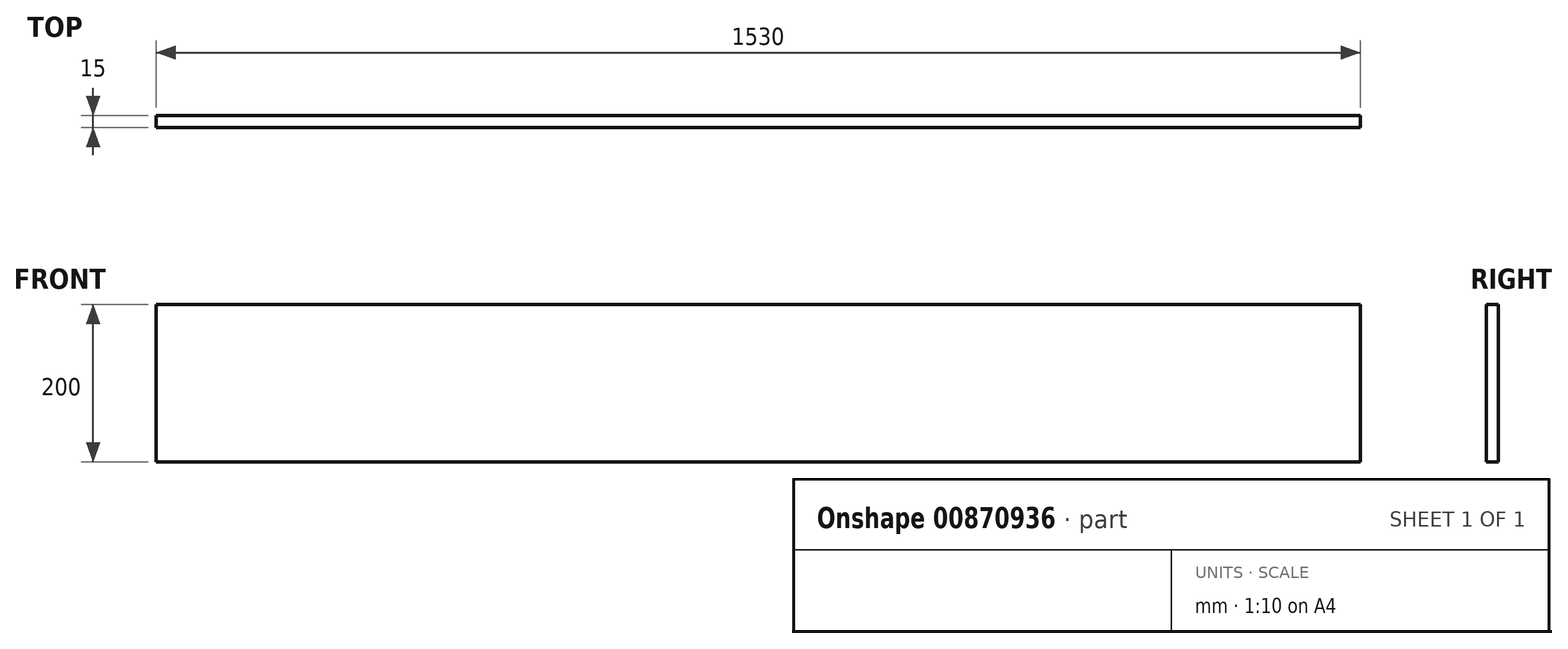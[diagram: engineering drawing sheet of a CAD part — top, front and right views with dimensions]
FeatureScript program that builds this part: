
annotation { "Feature Type Name" : "Feature", "Feature Type Description" : "" }
export const myFeature = defineFeature(function(context is Context, id is Id, definition is map)
    precondition{}
    {
        {
            var Q0;
            Q0=qCreatedBy(makeId("Front.planeOp"),FACE);
            var sketch = newSketch(context, id + "F0", { "sketchPlane" : qUnion([Q0])});
            skLineSegment(sketch, "E0.bottom", {"start": v(0, 0) * mm, "end": v(-1530, 0) * mm});
            skLineSegment(sketch, "E0.top", {"start": v(0, 200) * mm, "end": v(-1530, 200) * mm});
            skLineSegment(sketch, "E0.left", {"start": v(0, 0) * mm, "end": v(0, 200) * mm});
            skLineSegment(sketch, "E0.right", {"start": v(-1530, 0) * mm, "end": v(-1530, 200) * mm});
            skPoint(sketch, "E0.middle", {"position": v(-765, 100) * mm});
            skSolve(sketch);
        }
        {
            var Q0;
            Q0 = qSketchRegion(id + "F0", true);
            extrude(context, id + "F1", {"entities" : qUnion([Q0]), "depth" : 15 * mm, "offsetDistance" : 25 * mm});
        }
    });
